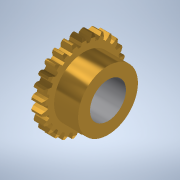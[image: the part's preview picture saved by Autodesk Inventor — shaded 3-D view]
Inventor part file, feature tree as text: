
AUTODESK INVENTOR PART (.ipt)
format: ipt  version: 2020.2 (Build 242310000, 310)  size: 406,528 bytes
history: native  units: mm
features: extrude x2, sketch x2
ambient origin geometry x8: Origin, YZ Plane, XZ Plane, XY Plane, X Axis, Y Axis, Z Axis, Center Point
bodies: Volumenkörper1 (feature_tree)
feature tree (4):
  extrude  "Extrusion1"  TaperAngle=0.0deg  [1 undecoded]
  extrude  "Extrusion2"  Depth=10.0mm TaperAngle=0.0deg
  sketch  "Sketch3"  dims[d8=4.0mm d9=0.0mm d10=0.0mm]
  sketch  "Sketch4"  dims[d11=6.0mm d12=10.0mm d13=0.0mm]
note: 1 required parameter value undecoded (feature->parameter linkage not recoverable at this tier; creation-order binding heuristic only, values carry confidence <= 0.55)
